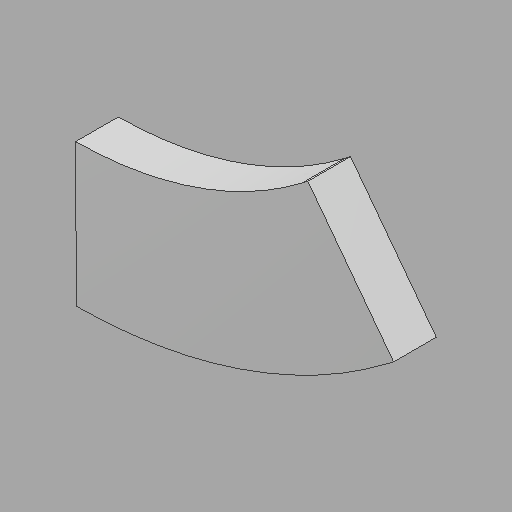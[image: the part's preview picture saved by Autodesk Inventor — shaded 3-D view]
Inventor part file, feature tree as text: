
AUTODESK INVENTOR PART (.ipt)
format: ipt  version: 2022.1 (Build 261234020, 234B)  size: 89,600 bytes
history: imported  units: in
note: dims shown in document units (in); Inventor stores cm internally (conversion verified against a paired STEP export)
features: imported_body x1
ambient origin geometry x8: Origin, YZ Plane, XZ Plane, XY Plane, X Axis, Y Axis, Z Axis, Center Point
bodies: Solid1 (imported_parasolid)
feature tree (1):
  imported_body  NMx_Import_Brep_tag  [imported B-rep: ~8 faces, bbox_mm=[1135.214774, 799.745127, 152.4]]
